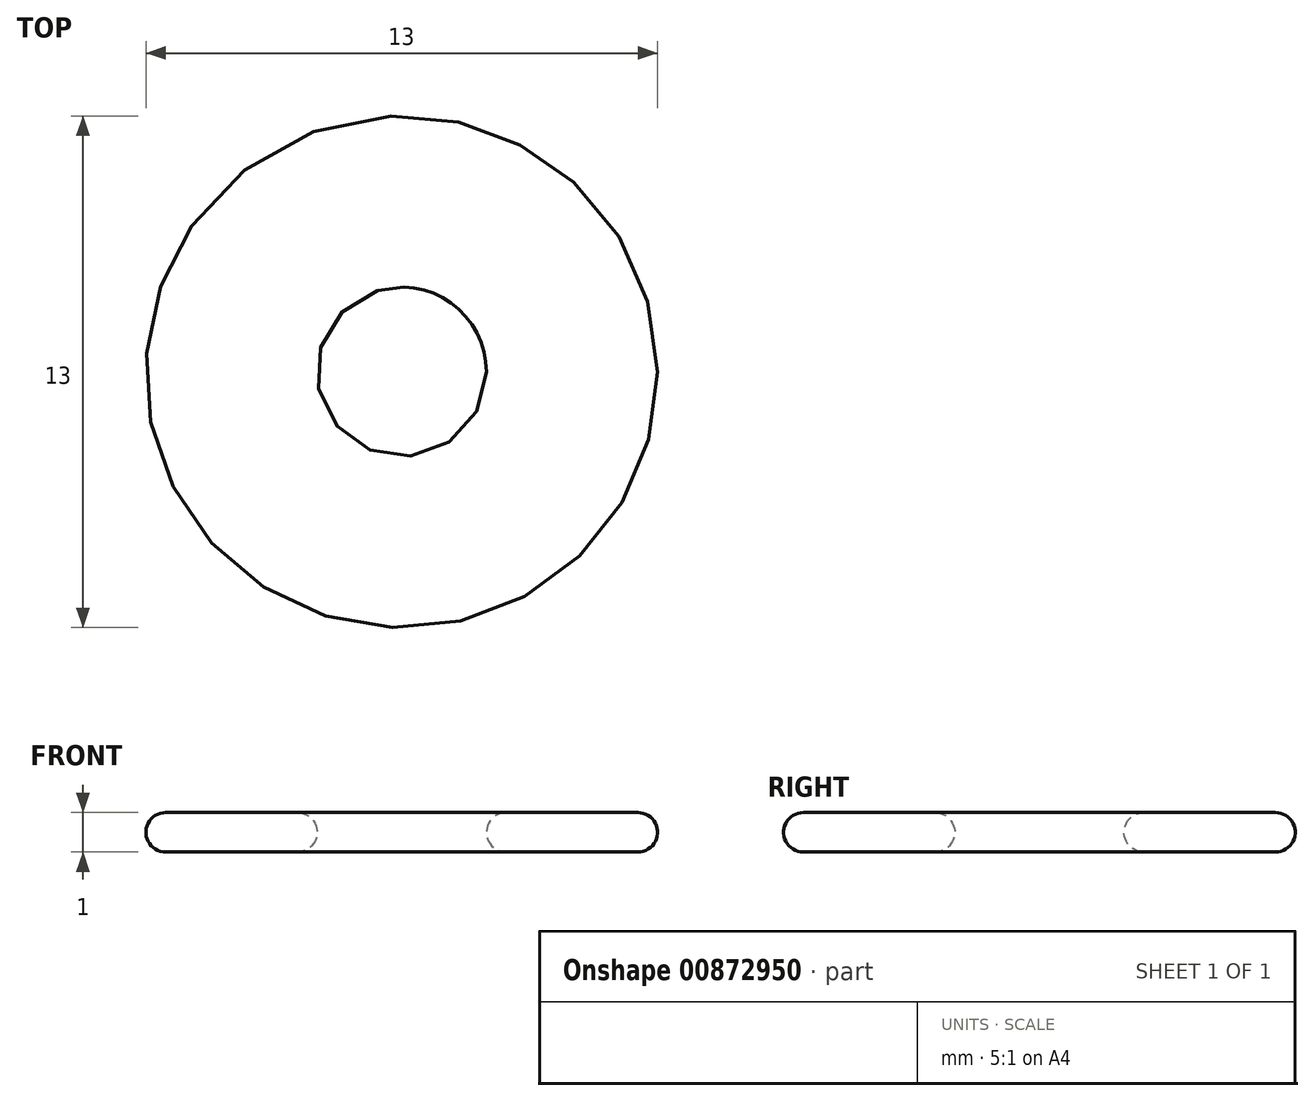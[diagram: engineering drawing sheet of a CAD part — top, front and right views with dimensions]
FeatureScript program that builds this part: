
annotation { "Feature Type Name" : "Feature", "Feature Type Description" : "" }
export const myFeature = defineFeature(function(context is Context, id is Id, definition is map)
    precondition{}
    {
        {
            var Q0;
            Q0=qCreatedBy(makeId("Top.planeOp"),FACE);
            var sketch = newSketch(context, id + "F0", { "sketchPlane" : qUnion([Q0])});
            skCircle(sketch, "E0", {"center": v(0, 0) * mm, "radius": 6.5 * mm});
            skCircle(sketch, "E1", {"center": v(0, 0) * mm, "radius": 2.15 * mm});
            skSolve(sketch);
        }
        {
            var Q0;
            Q0=makeQuery(id+"F0.imprint","IMPRINT",FACE,{"disambiguationData":[TD([[makeQuery(id+"F0.imprint","IMPRINT",EDGE,{"derivedFrom":sQuery(id+"F0.wireOp",EDGE,"E0")}),1.0]])]});
            extrude(context, id + "F1", {"entities" : qUnion([Q0]), "depth" : 1 * mm, "offsetDistance" : 25 * mm});
        }
        {
            var Q0;
            Q0=makeQuery(id+"F1.opExtrude","CAP_EDGE",EDGE,{"disambiguationData":[OSD([sQuery(id+"F0.wireOp",EDGE,"E0")])],"isStart":false});
            var Q1;
            Q1=makeQuery(id+"F1.opExtrude","CAP_FACE",FACE,{"disambiguationData":[OSD([sQuery(id+"F0.wireOp",EDGE,"E0"),sQuery(id+"F0.wireOp",EDGE,"E1")])],"isStart":false});
            var Q2;
            Q2=makeQuery(id+"F1.opExtrude","SWEPT_FACE",FACE,{"disambiguationData":[OSD([sQuery(id+"F0.wireOp",EDGE,"E0")])]});
            var Q3;
            Q3=makeQuery(id+"F1.opExtrude","CAP_EDGE",EDGE,{"disambiguationData":[OSD([sQuery(id+"F0.wireOp",EDGE,"E0")])],"isStart":true});
            var Q4;
            Q4=makeQuery(id+"F1.opExtrude","CAP_FACE",FACE,{"disambiguationData":[OSD([sQuery(id+"F0.wireOp",EDGE,"E0"),sQuery(id+"F0.wireOp",EDGE,"E1")])],"isStart":true});
            var Q5;
            Q5=makeQuery(id+"F1.opExtrude","SWEPT_FACE",FACE,{"disambiguationData":[OSD([sQuery(id+"F0.wireOp",EDGE,"E1")])]});
            var Q6;
            Q6=makeQuery(id+"F1.opExtrude","CAP_EDGE",EDGE,{"disambiguationData":[OSD([sQuery(id+"F0.wireOp",EDGE,"E1")])],"isStart":false});
            var Q7;
            Q7=makeQuery(id+"F1.opExtrude","CAP_EDGE",EDGE,{"disambiguationData":[OSD([sQuery(id+"F0.wireOp",EDGE,"E1")])],"isStart":true});
            fillet(context, id + "F2", {"entities" : qUnion([Q0, Q1, Q2, Q3, Q4, Q5, Q6, Q7]), "radius" : 0.5 * mm, "tangentPropagation" : true, "allowEdgeOverflow" : false});
        }
    });
